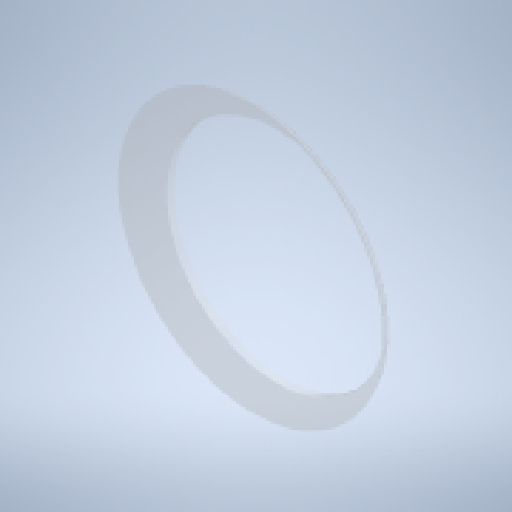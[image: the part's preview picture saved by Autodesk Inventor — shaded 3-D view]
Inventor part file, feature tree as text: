
AUTODESK INVENTOR PART (.ipt)
format: ipt  version: 2023 (Build 270158000, 158)  size: 276,480 bytes
history: native  units: mm
features: reference x6, other x3, fillet x2, extrude x1, sketch x1
ambient origin geometry x8: Origin, YZ Plane, XZ Plane, XY Plane, X Axis, Y Axis, Z Axis, Center Point
bodies: Body1 (feature_tree)
feature tree (13):
  extrude  "Estrusione2"  Depth=1.5mm TaperAngle=0.0deg
  fillet  "Raccordo3"  Radius=2.0mm
  fillet  "Raccordo4"  Radius=2.0mm
  sketch  "Schizzo2"
  reference  "Riferimento5"
  reference  "Riferimento6"
  reference  "Riferimento7"
  reference  "Riferimento8"
  reference  "Riferimento9"
  reference  "Riferimento10"
  other  "08-20-2023-assieme con riduttore.iam"
  other  "CE2_adaptor_thin_2_v7:1"
  other  "Sony_E-Mount_Body_Cap:1"
